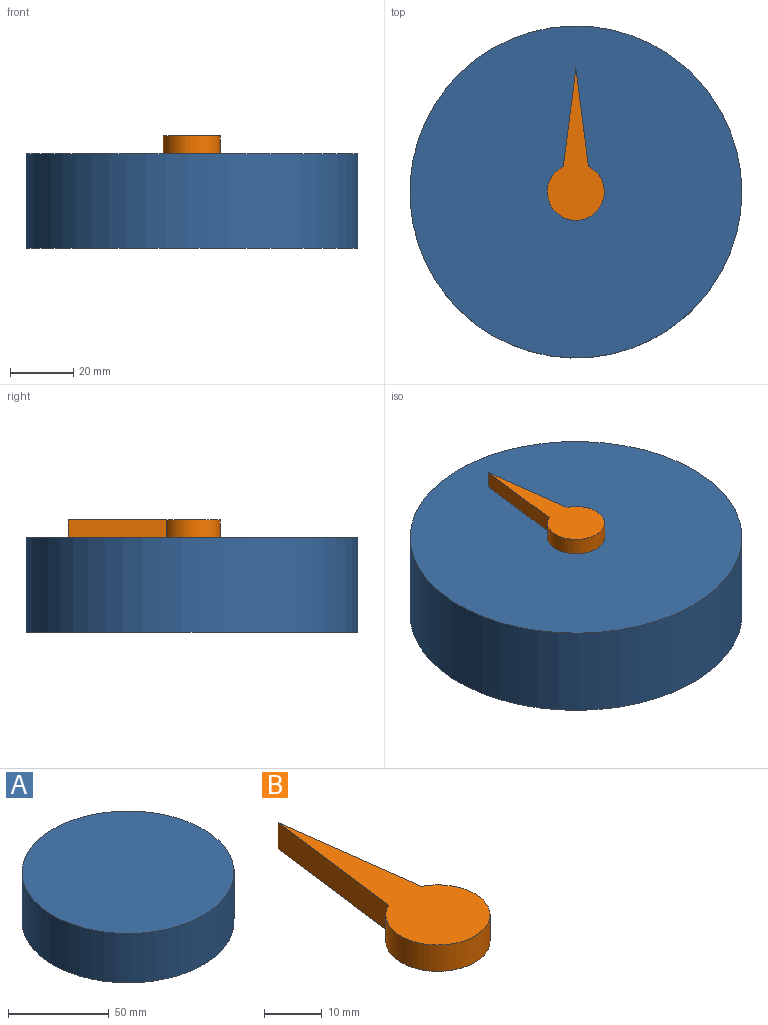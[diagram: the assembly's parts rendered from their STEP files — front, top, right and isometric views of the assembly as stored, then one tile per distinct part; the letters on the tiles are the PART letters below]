
ASSEMBLY  parts=2 mates=1
PART A: 3 faces, bbox 105.3x105.3x30 mm
  f0: cylinder r=52.63mm len=105.27mm, axis (0,0,-1), area 9912mm2, adj f1,f2
  f1: plane 105.27x105.27mm, normal (0,0,1), area 8703.3mm2, adj f0
  f2: plane 105.27x105.27mm, normal (0,0,-1), area 8703.3mm2, adj f0
PART B: 5 faces, bbox 18.1x48.2x5.6 mm
  f0: cylinder r=9.03mm len=18.07mm, axis (0,0,-1), area 271mm2, adj f1,f2,f3,f4
  f1: plane 31.1x5.59mm, normal (0.99,0.13,0), area 175.2mm2, adj f0,f2,f3,f4
  f2: plane 31.08x5.59mm, normal (-0.99,0.13,0), area 175.1mm2, adj f0,f1,f3,f4
  f3: plane 48.23x18.07mm, normal (0,0,1), area 375.5mm2, adj f0,f1,f2
  f4: plane 48.23x18.07mm, normal (0,0,-1), area 375.5mm2, adj f0,f1,f2
PLACE A at identity fixed
PLACE B at identity
MATE revolute A.f0 <-> B.f0  axis (0,0,1) through (0,0,29.97)mm
